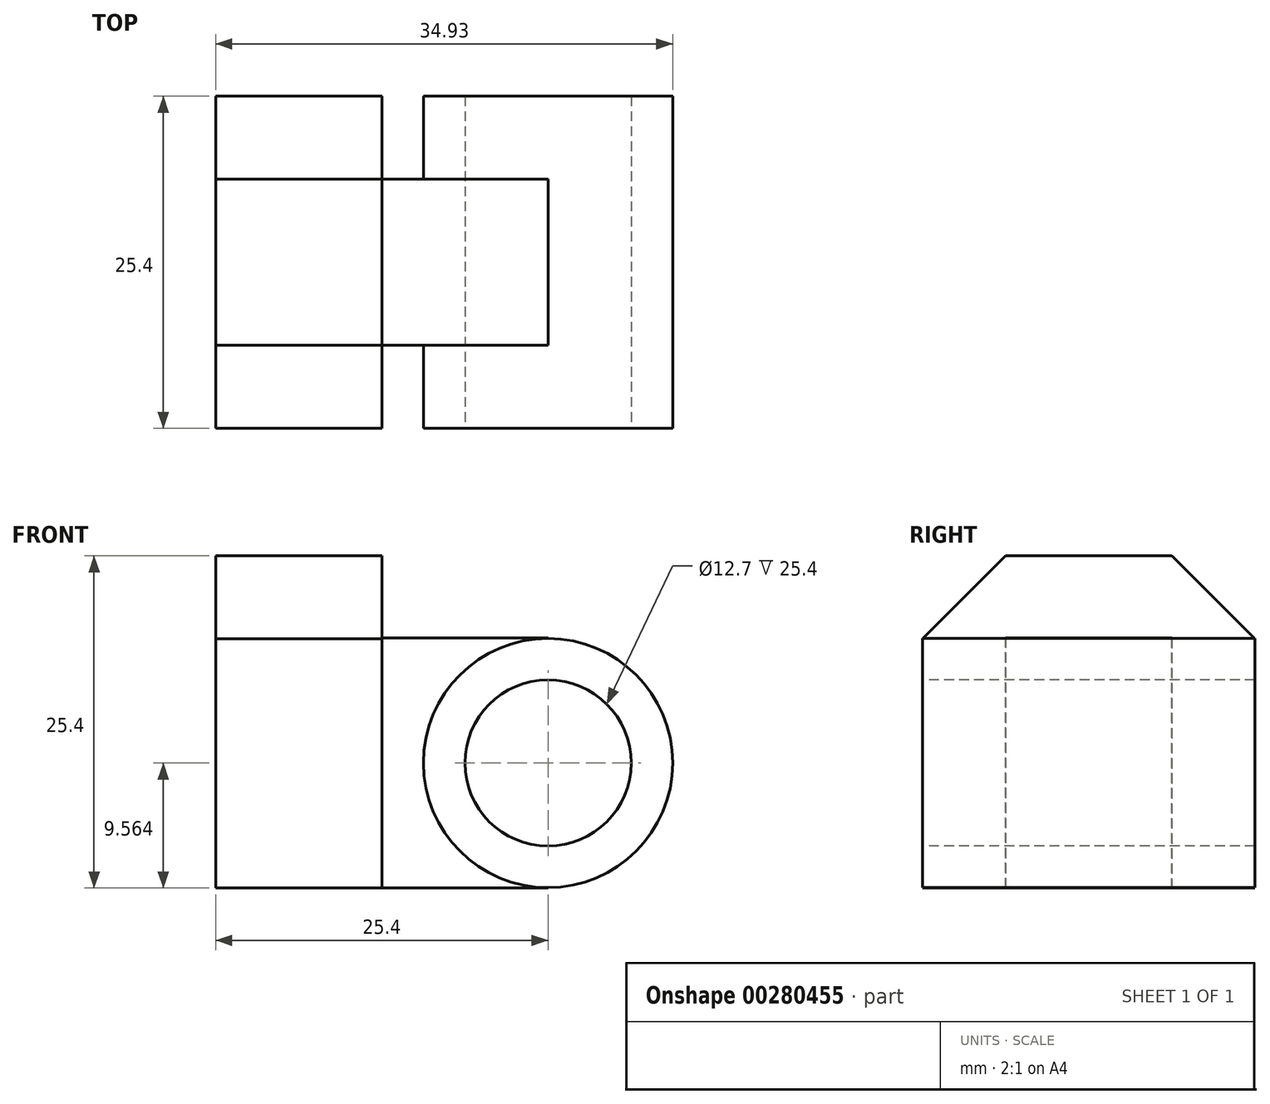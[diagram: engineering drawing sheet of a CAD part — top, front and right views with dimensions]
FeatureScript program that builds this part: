
annotation { "Feature Type Name" : "Feature", "Feature Type Description" : "" }
export const myFeature = defineFeature(function(context is Context, id is Id, definition is map)
    precondition{}
    {
        {
            var Q0;
            Q0=qCreatedBy(makeId("Top.planeOp"),FACE);
            var sketch = newSketch(context, id + "F0", { "sketchPlane" : qUnion([Q0])});
            skLineSegment(sketch, "E0.bottom", {"start": v(0, 0) * mm, "end": v(-12.7, 0) * mm});
            skLineSegment(sketch, "E0.top", {"start": v(0, 25.4) * mm, "end": v(-12.7, 25.4) * mm});
            skLineSegment(sketch, "E0.left", {"start": v(0, 0) * mm, "end": v(0, 25.4) * mm});
            skLineSegment(sketch, "E0.right", {"start": v(-12.7, 0) * mm, "end": v(-12.7, 25.4) * mm});
            skSolve(sketch);
        }
        {
            var Q0;
            Q0 = qSketchRegion(id + "F0", true);
            extrude(context, id + "F1", {"entities" : qUnion([Q0]), "depth" : 25.4 * mm});
        }
        {
            var Q0;
            Q0=makeQuery(id+"F1.opExtrude","SWEPT_FACE",FACE,{"disambiguationData":[OSD([sQuery(id+"F0.wireOp",EDGE,"E0.left")])]});
            var sketch = newSketch(context, id + "F2", { "sketchPlane" : qUnion([Q0])});
            skLineSegment(sketch, "E1", {"start": v(25.4, 25.4) * mm, "end": v(25.4, 19.05) * mm});
            skLineSegment(sketch, "E2", {"start": v(0, 19.05) * mm, "end": v(0, 25.4) * mm});
            skLineSegment(sketch, "E3", {"start": v(0, 25.4) * mm, "end": v(6.35, 25.4) * mm});
            skLineSegment(sketch, "E4", {"start": v(6.35, 25.4) * mm, "end": v(0, 19.05) * mm});
            skLineSegment(sketch, "E5", {"start": v(25.4, 25.4) * mm, "end": v(19.05, 25.4) * mm});
            skLineSegment(sketch, "E6", {"start": v(19.05, 25.4) * mm, "end": v(25.4, 19.05) * mm});
            skSolve(sketch);
        }
        {
            var Q0;
            Q0 = qSketchRegion(id + "F2", true);
            extrude(context, id + "F3", {"entities" : qUnion([Q0]), "operationType" : NewBodyOperationType.REMOVE, "endBound" : BoundingType.THROUGH_ALL, "oppositeDirection" : true, "depth" : 25.4 * mm});
        }
        {
            var Q0;
            Q0=makeQuery(id+"F1.opExtrude","SWEPT_FACE",FACE,{"disambiguationData":[OSD([sQuery(id+"F0.wireOp",EDGE,"E0.left")])]});
            var sketch = newSketch(context, id + "F4", { "sketchPlane" : qUnion([Q0])});
            skLineSegment(sketch, "E7", {"start": v(6.35, 19.13) * mm, "end": v(6.35, 0) * mm});
            skLineSegment(sketch, "E8", {"start": v(6.35, 0) * mm, "end": v(19.05, 0) * mm});
            skLineSegment(sketch, "E9", {"start": v(19.05, 0) * mm, "end": v(19.05, 19.13) * mm});
            skLineSegment(sketch, "E10", {"start": v(6.35, 19.13) * mm, "end": v(19.05, 19.13) * mm});
            skSolve(sketch);
        }
        {
            var Q0;
            Q0 = qSketchRegion(id + "F4", true);
            extrude(context, id + "F5", {"entities" : qUnion([Q0]), "operationType" : NewBodyOperationType.ADD, "depth" : 12.7 * mm});
        }
        {
            var Q0;
            Q0=makeQuery(id+"F5.opExtrude","SWEPT_FACE",FACE,{"disambiguationData":[OSD([sQuery(id+"F4.wireOp",EDGE,"E7")])]});
            var sketch = newSketch(context, id + "F6", { "sketchPlane" : qUnion([Q0])});
            skCircle(sketch, "E11", {"center": v(12.7, 9.56) * mm, "radius": 9.53 * mm});
            skSolve(sketch);
        }
        {
            var Q0;
            Q0 = qSketchRegion(id + "F6", true);
            extrude(context, id + "F7", {"entities" : qUnion([Q0]), "operationType" : NewBodyOperationType.ADD, "depth" : 6.35 * mm, "hasSecondDirection" : true, "secondDirectionOppositeDirection" : true, "secondDirectionDepth" : 19.05 * mm});
        }
        {
            var Q0;
            Q0=makeQuery(id+"F7.opExtrude","CAP_FACE",FACE,{"disambiguationData":[OSD([sQuery(id+"F6.wireOp",EDGE,"E11")])],"isStart":false});
            var sketch = newSketch(context, id + "F8", { "sketchPlane" : qUnion([Q0])});
            skCircle(sketch, "E12", {"center": v(12.7, 9.56) * mm, "radius": 6.35 * mm});
            skSolve(sketch);
        }
        {
            var Q0;
            Q0 = qSketchRegion(id + "F8", true);
            extrude(context, id + "F9", {"entities" : qUnion([Q0]), "operationType" : NewBodyOperationType.REMOVE, "endBound" : BoundingType.THROUGH_ALL, "oppositeDirection" : true, "depth" : 25.4 * mm});
        }
    });
